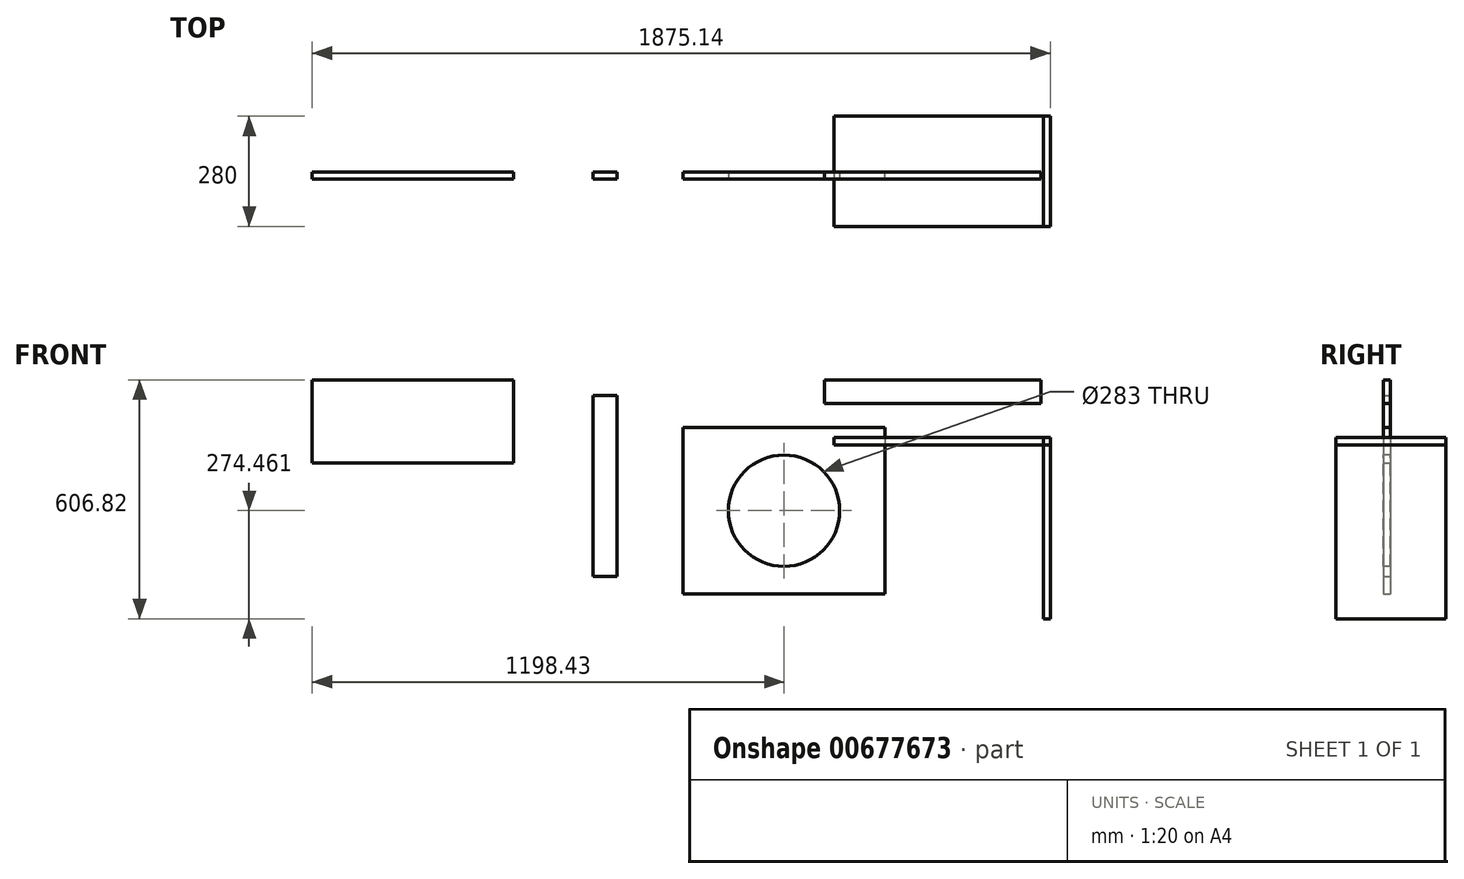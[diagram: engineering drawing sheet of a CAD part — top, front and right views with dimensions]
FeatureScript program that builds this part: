
annotation { "Feature Type Name" : "Feature", "Feature Type Description" : "" }
export const myFeature = defineFeature(function(context is Context, id is Id, definition is map)
    precondition{}
    {
        {
            var Q0;
            Q0=qCreatedBy(makeId("Right.planeOp"),FACE);
            var sketch = newSketch(context, id + "F0", { "sketchPlane" : qUnion([Q0])});
            skLineSegment(sketch, "E0.bottom", {"start": v(-138.6, 352.72) * mm, "end": v(141.4, 352.72) * mm});
            skLineSegment(sketch, "E0.top", {"start": v(-138.6, -107.28) * mm, "end": v(141.4, -107.28) * mm});
            skLineSegment(sketch, "E0.left", {"start": v(-138.6, 352.72) * mm, "end": v(-138.6, -107.28) * mm});
            skLineSegment(sketch, "E0.right", {"start": v(141.4, 352.72) * mm, "end": v(141.4, -107.28) * mm});
            skSolve(sketch);
        }
        {
            var Q0;
            Q0=makeQuery(id+"F0.imprint","IMPRINT",FACE,{"disambiguationData":[TD([[makeQuery(id+"F0.imprint","IMPRINT",EDGE,{"derivedFrom":sQuery(id+"F0.wireOp",EDGE,"E0.bottom")}),-1.0]])]});
            extrude(context, id + "F1", {"entities" : qUnion([Q0]), "depth" : 18 * mm, "offsetDistance" : 25 * mm});
        }
        {
            var Q0;
            Q0=makeQuery(id+"F1.opExtrude","SWEPT_FACE",FACE,{"disambiguationData":[OSD([sQuery(id+"F0.wireOp",EDGE,"E0.bottom")])]});
            var sketch = newSketch(context, id + "F2", { "sketchPlane" : qUnion([Q0])});
            skLineSegment(sketch, "E1.bottom", {"start": v(18, 141.4) * mm, "end": v(-532, 141.4) * mm});
            skLineSegment(sketch, "E1.top", {"start": v(18, -138.6) * mm, "end": v(-532, -138.6) * mm});
            skLineSegment(sketch, "E1.left", {"start": v(18, 141.4) * mm, "end": v(18, -138.6) * mm});
            skLineSegment(sketch, "E1.right", {"start": v(-532, 141.4) * mm, "end": v(-532, -138.6) * mm});
            skSolve(sketch);
        }
        {
            var Q0;
            Q0 = qSketchRegion(id + "F2", true);
            extrude(context, id + "F3", {"entities" : qUnion([Q0]), "oppositeDirection" : true, "depth" : 18 * mm, "offsetDistance" : 25 * mm});
        }
        {
            var Q0;
            Q0=qCreatedBy(makeId("Front.planeOp"),FACE);
            var sketch = newSketch(context, id + "F4", { "sketchPlane" : qUnion([Q0])});
            skLineSegment(sketch, "E2.bottom", {"start": v(-555.81, 499.54) * mm, "end": v(-5.81, 499.54) * mm});
            skLineSegment(sketch, "E2.top", {"start": v(-555.81, 439.54) * mm, "end": v(-5.81, 439.54) * mm});
            skLineSegment(sketch, "E2.left", {"start": v(-555.81, 499.54) * mm, "end": v(-555.81, 439.54) * mm});
            skLineSegment(sketch, "E2.right", {"start": v(-5.81, 499.54) * mm, "end": v(-5.81, 439.54) * mm});
            skSolve(sketch);
        }
        {
            var Q0;
            Q0 = qSketchRegion(id + "F4", true);
            extrude(context, id + "F5", {"entities" : qUnion([Q0]), "depth" : 18 * mm, "offsetDistance" : 25 * mm});
        }
        {
            var Q0;
            Q0=qCreatedBy(makeId("Front.planeOp"),FACE);
            var sketch = newSketch(context, id + "F6", { "sketchPlane" : qUnion([Q0])});
            skLineSegment(sketch, "E3.bottom", {"start": v(-1143.3, 460.04) * mm, "end": v(-1083.3, 460.04) * mm});
            skLineSegment(sketch, "E3.top", {"start": v(-1143.3, 0.04) * mm, "end": v(-1083.3, 0.04) * mm});
            skLineSegment(sketch, "E3.left", {"start": v(-1143.3, 460.04) * mm, "end": v(-1143.3, 0.04) * mm});
            skLineSegment(sketch, "E3.right", {"start": v(-1083.3, 460.04) * mm, "end": v(-1083.3, 0.04) * mm});
            skSolve(sketch);
        }
        {
            var Q0;
            Q0 = qSketchRegion(id + "F6", true);
            extrude(context, id + "F7", {"entities" : qUnion([Q0]), "depth" : 18 * mm, "offsetDistance" : 25 * mm});
        }
        {
            var Q0;
            Q0=qCreatedBy(makeId("Front.planeOp"),FACE);
            var sketch = newSketch(context, id + "F8", { "sketchPlane" : qUnion([Q0])});
            skLineSegment(sketch, "E4.bottom", {"start": v(-1566.41, 384.47) * mm, "end": v(-1541.41, 384.47) * mm});
            skLineSegment(sketch, "E4.top", {"start": v(-1566.41, -37.53) * mm, "end": v(-1541.41, -37.53) * mm});
            skLineSegment(sketch, "E4.left", {"start": v(-1566.41, 384.47) * mm, "end": v(-1566.41, -37.53) * mm});
            skLineSegment(sketch, "E4.right", {"start": v(-1541.41, 384.47) * mm, "end": v(-1541.41, -37.53) * mm});
            skSolve(sketch);
        }
        {
            var Q0;
            Q0 = qSketchRegion(id + "F8", true);
            extrude(context, id + "F9", {"entities" : qUnion([Q0]), "depth" : 18 * mm, "offsetDistance" : 25 * mm});
        }
        {
            var Q0;
            Q0=qCreatedBy(makeId("Front.planeOp"),FACE);
            var sketch = newSketch(context, id + "F10", { "sketchPlane" : qUnion([Q0])});
            skLineSegment(sketch, "E5.bottom", {"start": v(-1497.77, 605.36) * mm, "end": v(-1035.77, 605.36) * mm});
            skLineSegment(sketch, "E5.top", {"start": v(-1497.77, 580.36) * mm, "end": v(-1035.77, 580.36) * mm});
            skLineSegment(sketch, "E5.left", {"start": v(-1497.77, 605.36) * mm, "end": v(-1497.77, 580.36) * mm});
            skLineSegment(sketch, "E5.right", {"start": v(-1035.77, 605.36) * mm, "end": v(-1035.77, 580.36) * mm});
            skSolve(sketch);
        }
        {
            var Q0;
            Q0 = qSketchRegion(id + "F10", true);
            extrude(context, id + "F11", {"entities" : qUnion([Q0]), "depth" : 18 * mm, "offsetDistance" : 25 * mm});
        }
        {
            var Q0;
            Q0=makeQuery(id+"F9.opExtrude","SWEPT_BODY",BODY,{"disambiguationData":[OSD([sQuery(id+"F8.wireOp",EDGE,"E4.bottom"),sQuery(id+"F8.wireOp",EDGE,"E4.top"),sQuery(id+"F8.wireOp",EDGE,"E4.left"),sQuery(id+"F8.wireOp",EDGE,"E4.right")])]});
            var Q1;
            Q1=makeQuery(id+"F11.opExtrude","SWEPT_BODY",BODY,{"disambiguationData":[OSD([sQuery(id+"F10.wireOp",EDGE,"E5.bottom"),sQuery(id+"F10.wireOp",EDGE,"E5.top"),sQuery(id+"F10.wireOp",EDGE,"E5.left"),sQuery(id+"F10.wireOp",EDGE,"E5.right")])]});
            deleteBodies(context, id + "F12", {"entities" : qUnion([Q0, Q1])});
        }
        {
            var Q0;
            Q0=qCreatedBy(makeId("Front.planeOp"),FACE);
            var sketch = newSketch(context, id + "F13", { "sketchPlane" : qUnion([Q0])});
            skLineSegment(sketch, "E6.bottom", {"start": v(-1857.14, 499.26) * mm, "end": v(-1345.14, 499.26) * mm});
            skLineSegment(sketch, "E6.top", {"start": v(-1857.14, 288.26) * mm, "end": v(-1345.14, 288.26) * mm});
            skLineSegment(sketch, "E6.left", {"start": v(-1857.14, 499.26) * mm, "end": v(-1857.14, 288.26) * mm});
            skLineSegment(sketch, "E6.right", {"start": v(-1345.14, 499.26) * mm, "end": v(-1345.14, 288.26) * mm});
            skSolve(sketch);
        }
        {
            var Q0;
            Q0 = qSketchRegion(id + "F13", true);
            extrude(context, id + "F14", {"entities" : qUnion([Q0]), "depth" : 18 * mm, "offsetDistance" : 25 * mm});
        }
        {
            var Q0;
            Q0=qCreatedBy(makeId("Front.planeOp"),FACE);
            var sketch = newSketch(context, id + "F15", { "sketchPlane" : qUnion([Q0])});
            skLineSegment(sketch, "E7.bottom", {"start": v(-914.7, 378.18) * mm, "end": v(-402.7, 378.18) * mm});
            skLineSegment(sketch, "E7.top", {"start": v(-914.7, -43.82) * mm, "end": v(-402.7, -43.82) * mm});
            skLineSegment(sketch, "E7.left", {"start": v(-914.7, 378.18) * mm, "end": v(-914.7, -43.82) * mm});
            skLineSegment(sketch, "E7.right", {"start": v(-402.7, 378.18) * mm, "end": v(-402.7, -43.82) * mm});
            skSolve(sketch);
        }
        {
            var Q0;
            Q0 = qSketchRegion(id + "F15", true);
            extrude(context, id + "F16", {"entities" : qUnion([Q0]), "depth" : 18 * mm, "offsetDistance" : 25 * mm});
        }
        {
            var Q0;
            Q0=makeQuery(id+"F16.opExtrude","CAP_FACE",FACE,{"disambiguationData":[OSD([sQuery(id+"F15.wireOp",EDGE,"E7.bottom"),sQuery(id+"F15.wireOp",EDGE,"E7.top"),sQuery(id+"F15.wireOp",EDGE,"E7.left"),sQuery(id+"F15.wireOp",EDGE,"E7.right")])],"isStart":false});
            var sketch = newSketch(context, id + "F17", { "sketchPlane" : qUnion([Q0])});
            skLineSegment(sketch, "E8", {"start": v(-914.7, 378.18) * mm, "end": v(-402.7, -43.82) * mm, "construction": true});
            skLineSegment(sketch, "E9", {"start": v(-402.7, 378.18) * mm, "end": v(-914.7, -43.82) * mm, "construction": true});
            skCircle(sketch, "E10", {"center": v(-658.7, 167.18) * mm, "radius": 141.5 * mm});
            skSolve(sketch);
        }
        {
            var Q0;
            Q0 = qSketchRegion(id + "F17", true);
            extrude(context, id + "F18", {"entities" : qUnion([Q0]), "operationType" : NewBodyOperationType.REMOVE, "endBound" : BoundingType.THROUGH_ALL, "oppositeDirection" : true, "depth" : 25 * mm, "offsetDistance" : 25 * mm});
        }
    });
